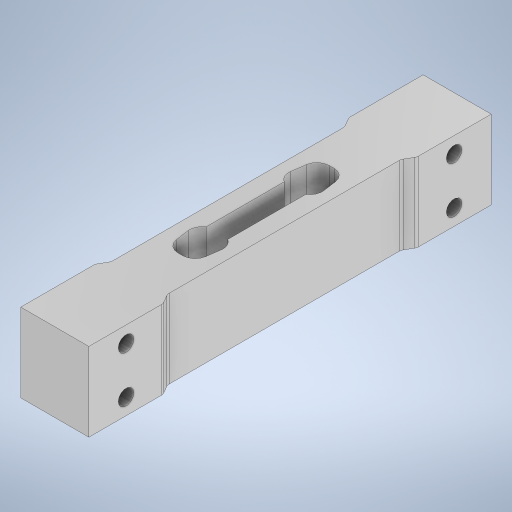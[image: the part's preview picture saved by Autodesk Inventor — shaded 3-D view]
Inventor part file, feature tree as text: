
AUTODESK INVENTOR PART (.ipt)
format: ipt  version: 2023 (Build 270158000, 158)  size: 336,384 bytes
history: native  units: mm
features: sketch x2, other x1, extrude x1, hole x1
ambient origin geometry x8: Origin, YZ Plane, XZ Plane, XY Plane, X Axis, Y Axis, Z Axis, Center Point
bodies: Body1 (feature_tree)
feature tree (5):
  other  "Sólido1"
  extrude  "Extrusão1"  Depth=22.0mm
  hole  "Furo1"  [1 undecoded]
  sketch  "Esboço1"  dims[d0=22.0mm d1=24.0mm]
  sketch  "Esboço2"  dims[d4=3.8mm d6=3.8mm d7=24.0mm d8=18.2mm d10=0.0mm d11=130.0mm d12=1.9mm d13=2.0mm d14=2.0mm d38=7.0mm d39=7.0mm d40=4.495648mm d41=4.495648mm d42=4.451897mm d43=0.625673mm d44=30.019663mm d45=1.545706mm d46=1.545706mm d47=0.625673mm d48=4.451897mm d49=3.961072mm d50=3.443308mm d51=9.467851mm d52=3.961072mm d53=3.960192mm d54=1.859599mm d55=4.451897mm d56=3.960192mm d57=3.960192mm d58=4.375069mm d59=1.859599mm d60=3.961072mm d61=3.961072mm d62=3.443308mm d63=3.443308mm d64=0.0mm d65=48.903794mm d67=0.0mm d68=25.4mm d69=0.0mm d70=15.0mm d72=25.4mm d73=5.2mm d74=0.0mm d75=12.0mm d76=15.0mm d77=12.0mm d78=0.0mm d79=5.2mm d80=5.0mm d81=6.0mm d82=3.023mm d83=2.0mm d84=14.3117mm d85=0.5mm d86=20.594885mm]
note: 1 required parameter value undecoded (feature->parameter linkage not recoverable at this tier; creation-order binding heuristic only, values carry confidence <= 0.55)
